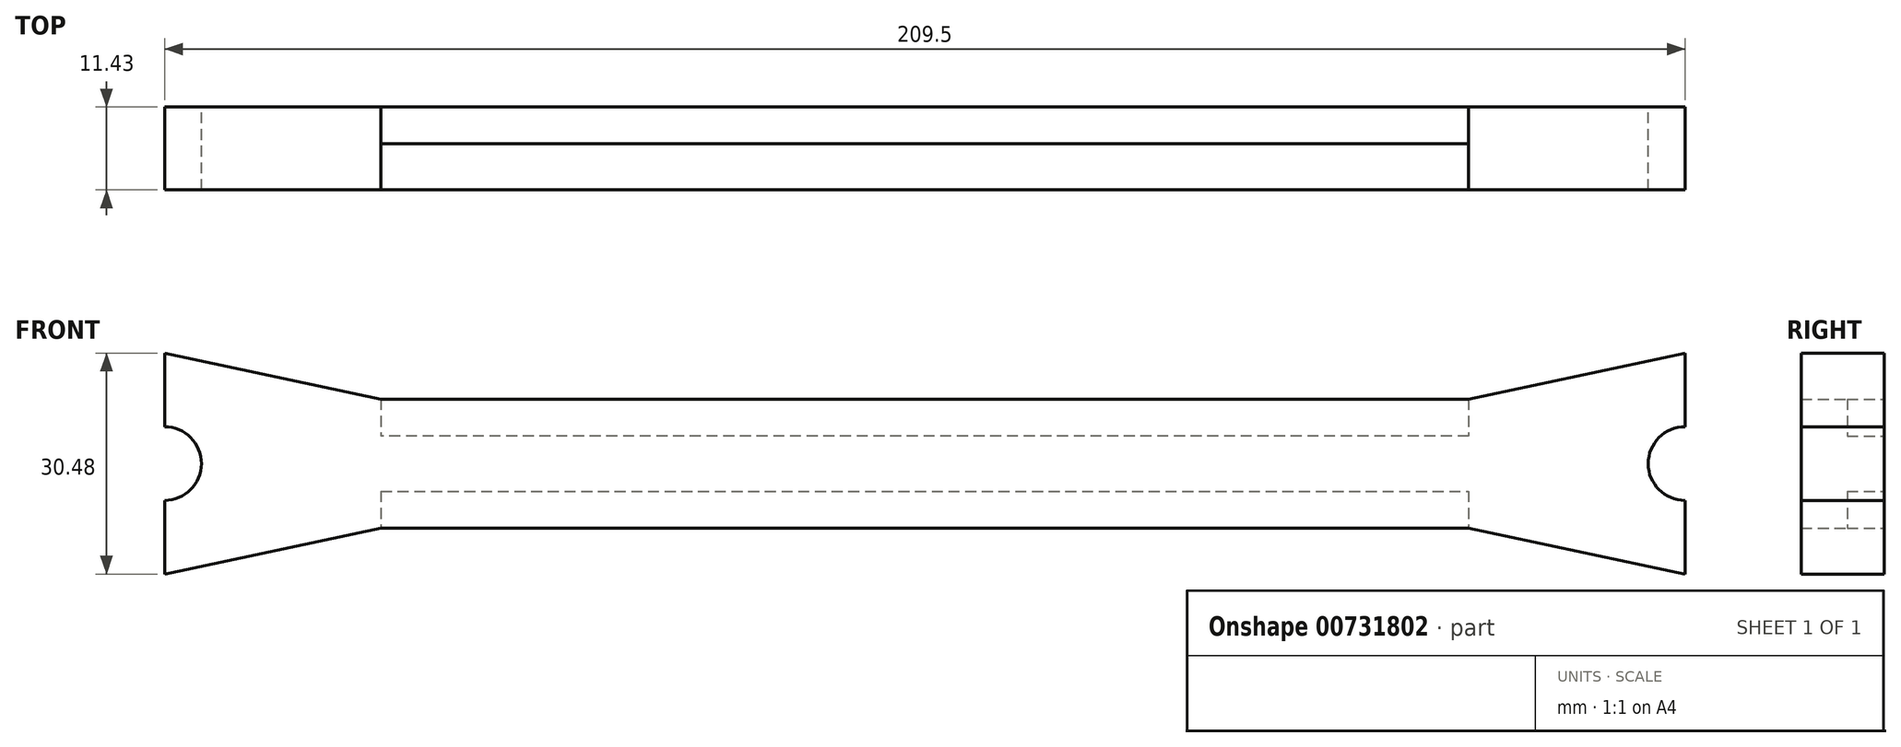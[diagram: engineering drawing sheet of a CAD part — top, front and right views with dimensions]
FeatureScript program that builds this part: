
annotation { "Feature Type Name" : "Feature", "Feature Type Description" : "" }
export const myFeature = defineFeature(function(context is Context, id is Id, definition is map)
    precondition{}
    {
        {
            var Q0;
            Q0=qCreatedBy(makeId("Front.planeOp"),FACE);
            var sketch = newSketch(context, id + "F0", { "sketchPlane" : qUnion([Q0])});
            skLineSegment(sketch, "E0", {"start": v(9.71, 24.9) * mm, "end": v(-140.15, 24.9) * mm});
            skLineSegment(sketch, "E1", {"start": v(-140.15, 42.68) * mm, "end": v(9.71, 42.68) * mm});
            skLineSegment(sketch, "E2", {"start": v(9.71, 42.68) * mm, "end": v(9.71, 24.9) * mm});
            skLineSegment(sketch, "E3", {"start": v(-140.15, 42.68) * mm, "end": v(-140.15, 24.9) * mm});
            skLineSegment(sketch, "E4", {"start": v(-140.15, 33.79) * mm, "end": v(-169.97, 33.79) * mm});
            skCircle(sketch, "E5", {"center": v(-169.97, 33.79) * mm, "radius": 15.24 * mm});
            skLineSegment(sketch, "E6", {"start": v(-169.97, 33.79) * mm, "end": v(-169.97, 18.55) * mm});
            skLineSegment(sketch, "E7", {"start": v(-169.97, 18.55) * mm, "end": v(-169.97, 49.03) * mm});
            skLineSegment(sketch, "E8", {"start": v(-169.97, 18.55) * mm, "end": v(-140.15, 24.9) * mm});
            skLineSegment(sketch, "E9", {"start": v(9.71, 33.79) * mm, "end": v(39.53, 33.79) * mm});
            skCircle(sketch, "E10", {"center": v(39.53, 33.79) * mm, "radius": 15.24 * mm});
            skLineSegment(sketch, "E11", {"start": v(39.53, 33.79) * mm, "end": v(39.53, 18.55) * mm});
            skLineSegment(sketch, "E12", {"start": v(39.53, 18.55) * mm, "end": v(39.53, 49.03) * mm});
            skLineSegment(sketch, "E13", {"start": v(39.53, 49.03) * mm, "end": v(9.71, 42.68) * mm});
            skLineSegment(sketch, "E14", {"start": v(39.53, 18.55) * mm, "end": v(9.71, 24.9) * mm});
            skLineSegment(sketch, "E15", {"start": v(-169.97, 49.03) * mm, "end": v(-140.15, 42.68) * mm});
            skLineSegment(sketch, "E16", {"start": v(-169.97, 33.79) * mm, "end": v(-157.27, 33.79) * mm});
            skLineSegment(sketch, "E17", {"start": v(-157.27, 33.79) * mm, "end": v(-157.27, 29.98) * mm});
            skLineSegment(sketch, "E18", {"start": v(-157.27, 29.98) * mm, "end": v(-157.27, 37.6) * mm});
            skLineSegment(sketch, "E19", {"start": v(-157.27, 37.6) * mm, "end": v(-120.77, 37.6) * mm});
            skLineSegment(sketch, "E20", {"start": v(-157.27, 29.98) * mm, "end": v(-120.77, 29.98) * mm});
            skLineSegment(sketch, "E21", {"start": v(39.53, 33.79) * mm, "end": v(26.83, 33.79) * mm});
            skLineSegment(sketch, "E22", {"start": v(26.83, 33.79) * mm, "end": v(26.83, 29.98) * mm});
            skLineSegment(sketch, "E23", {"start": v(26.83, 29.98) * mm, "end": v(26.83, 37.6) * mm});
            skLineSegment(sketch, "E24", {"start": v(26.83, 37.6) * mm, "end": v(-120.77, 37.6) * mm});
            skLineSegment(sketch, "E25", {"start": v(-120.77, 29.98) * mm, "end": v(26.83, 29.98) * mm});
            skCircle(sketch, "E26", {"center": v(39.53, 33.79) * mm, "radius": 5.08 * mm});
            skCircle(sketch, "E27", {"center": v(-169.97, 33.79) * mm, "radius": 5.08 * mm});
            skSolve(sketch);
        }
        {
            var Q0;
            {var subQ0=sQuery(id+"F0.wireOp",EDGE,"E7");var subQ4=sQuery(id+"F0.wireOp",EDGE,"E27");var subQ5=makeQuery(id+"F0.imprint","INTERSECT",VERTEX,{"disambiguationData":[OD(0.0)],"derivedFrom":[subQ0,subQ4]});Q0=makeQuery(id+"F0.imprint","IMPRINT",FACE,{"disambiguationData":[TD([[makeQuery(id+"F0.imprint","IMPRINT",EDGE,{"disambiguationData":[TD([[subQ5,1.0]])],"derivedFrom":subQ4}),-1.0]])]});}
            var Q1;
            {var subQ7=sQuery(id+"F0.wireOp",EDGE,"E15");var subQ8=sQuery(id+"F0.wireOp",EDGE,"E5");var subQ10=makeQuery(id+"F0.imprint","INTERSECT",VERTEX,{"derivedFrom":[subQ8,subQ7]});Q1=makeQuery(id+"F0.imprint","IMPRINT",FACE,{"disambiguationData":[TD([[makeQuery(id+"F0.imprint","IMPRINT",EDGE,{"disambiguationData":[TD([[subQ10,1.0]])],"derivedFrom":subQ8}),1.0]])]});}
            var Q2;
            {var subQ5=sQuery(id+"F0.wireOp",EDGE,"E8");var subQ7=sQuery(id+"F0.wireOp",EDGE,"E5");var subQ9=makeQuery(id+"F0.imprint","INTERSECT",VERTEX,{"derivedFrom":[subQ7,subQ5]});Q2=makeQuery(id+"F0.imprint","IMPRINT",FACE,{"disambiguationData":[TD([[makeQuery(id+"F0.imprint","IMPRINT",EDGE,{"disambiguationData":[TD([[subQ9,-1.0]])],"derivedFrom":subQ7}),1.0]])]});}
            var Q3;
            {var subQ1=sQuery(id+"F0.wireOp",EDGE,"E4");var subQ3=sQuery(id+"F0.wireOp",EDGE,"E5");var subQ4=makeQuery(id+"F0.imprint","INTERSECT",VERTEX,{"derivedFrom":[subQ1,subQ3]});Q3=makeQuery(id+"F0.imprint","IMPRINT",FACE,{"disambiguationData":[TD([[makeQuery(id+"F0.imprint","IMPRINT",EDGE,{"disambiguationData":[TD([[subQ4,-1.0]])],"derivedFrom":subQ3}),1.0]])]});}
            var Q4;
            {var subQ1=sQuery(id+"F0.wireOp",EDGE,"E4");var subQ3=sQuery(id+"F0.wireOp",EDGE,"E5");var subQ4=makeQuery(id+"F0.imprint","INTERSECT",VERTEX,{"derivedFrom":[subQ1,subQ3]});Q4=makeQuery(id+"F0.imprint","IMPRINT",FACE,{"disambiguationData":[TD([[makeQuery(id+"F0.imprint","IMPRINT",EDGE,{"disambiguationData":[TD([[subQ4,1.0]])],"derivedFrom":subQ3}),1.0]])]});}
            var Q5;
            {var subQ0=sQuery(id+"F0.wireOp",EDGE,"E4");var subQ1=sQuery(id+"F0.wireOp",EDGE,"E3");var subQ2=makeQuery(id+"F0.imprint","INTERSECT",VERTEX,{"derivedFrom":[subQ1,subQ0]});Q5=makeQuery(id+"F0.imprint","IMPRINT",FACE,{"disambiguationData":[TD([[makeQuery(id+"F0.imprint","IMPRINT",EDGE,{"disambiguationData":[TD([[subQ2,-1.0]])],"derivedFrom":subQ1}),-1.0]])]});}
            var Q6;
            {var subQ0=sQuery(id+"F0.wireOp",EDGE,"E4");var subQ1=sQuery(id+"F0.wireOp",EDGE,"E3");var subQ2=makeQuery(id+"F0.imprint","INTERSECT",VERTEX,{"derivedFrom":[subQ1,subQ0]});Q6=makeQuery(id+"F0.imprint","IMPRINT",FACE,{"disambiguationData":[TD([[makeQuery(id+"F0.imprint","IMPRINT",EDGE,{"disambiguationData":[TD([[subQ2,1.0]])],"derivedFrom":subQ1}),-1.0]])]});}
            var Q7;
            {var subQ4=sQuery(id+"F0.wireOp",EDGE,"E2");var subQ5=makeQuery(id+"F0.imprint","INTERSECT",VERTEX,{"derivedFrom":[subQ4,sQuery(id+"F0.wireOp",EDGE,"E9")]});Q7=makeQuery(id+"F0.imprint","IMPRINT",FACE,{"disambiguationData":[TD([[makeQuery(id+"F0.imprint","IMPRINT",EDGE,{"disambiguationData":[TD([[subQ5,1.0]])],"derivedFrom":subQ4}),-1.0]])]});}
            var Q8;
            {var subQ0=sQuery(id+"F0.wireOp",EDGE,"E9");var subQ1=sQuery(id+"F0.wireOp",EDGE,"E2");var subQ2=makeQuery(id+"F0.imprint","INTERSECT",VERTEX,{"derivedFrom":[subQ1,subQ0]});Q8=makeQuery(id+"F0.imprint","IMPRINT",FACE,{"disambiguationData":[TD([[makeQuery(id+"F0.imprint","IMPRINT",EDGE,{"disambiguationData":[TD([[subQ2,1.0]])],"derivedFrom":subQ1}),1.0]])]});}
            var Q9;
            {var subQ0=sQuery(id+"F0.wireOp",EDGE,"E9");var subQ1=sQuery(id+"F0.wireOp",EDGE,"E2");var subQ2=makeQuery(id+"F0.imprint","INTERSECT",VERTEX,{"derivedFrom":[subQ1,subQ0]});Q9=makeQuery(id+"F0.imprint","IMPRINT",FACE,{"disambiguationData":[TD([[makeQuery(id+"F0.imprint","IMPRINT",EDGE,{"disambiguationData":[TD([[subQ2,-1.0]])],"derivedFrom":subQ1}),1.0]])]});}
            var Q10;
            {var subQ1=sQuery(id+"F0.wireOp",EDGE,"E9");var subQ3=sQuery(id+"F0.wireOp",EDGE,"E10");var subQ4=makeQuery(id+"F0.imprint","INTERSECT",VERTEX,{"derivedFrom":[subQ1,subQ3]});Q10=makeQuery(id+"F0.imprint","IMPRINT",FACE,{"disambiguationData":[TD([[makeQuery(id+"F0.imprint","IMPRINT",EDGE,{"disambiguationData":[TD([[subQ4,1.0]])],"derivedFrom":subQ3}),1.0]])]});}
            var Q11;
            {var subQ1=sQuery(id+"F0.wireOp",EDGE,"E9");var subQ3=sQuery(id+"F0.wireOp",EDGE,"E10");var subQ4=makeQuery(id+"F0.imprint","INTERSECT",VERTEX,{"derivedFrom":[subQ1,subQ3]});Q11=makeQuery(id+"F0.imprint","IMPRINT",FACE,{"disambiguationData":[TD([[makeQuery(id+"F0.imprint","IMPRINT",EDGE,{"disambiguationData":[TD([[subQ4,-1.0]])],"derivedFrom":subQ3}),1.0]])]});}
            var Q12;
            {var subQ5=sQuery(id+"F0.wireOp",EDGE,"E13");var subQ7=sQuery(id+"F0.wireOp",EDGE,"E10");var subQ10=makeQuery(id+"F0.imprint","INTERSECT",VERTEX,{"derivedFrom":[subQ7,subQ5]});Q12=makeQuery(id+"F0.imprint","IMPRINT",FACE,{"disambiguationData":[TD([[makeQuery(id+"F0.imprint","IMPRINT",EDGE,{"disambiguationData":[TD([[subQ10,-1.0]])],"derivedFrom":subQ7}),1.0]])]});}
            var Q13;
            {var subQ0=sQuery(id+"F0.wireOp",EDGE,"E12");var subQ4=sQuery(id+"F0.wireOp",EDGE,"E26");var subQ5=makeQuery(id+"F0.imprint","INTERSECT",VERTEX,{"disambiguationData":[OD(0.0)],"derivedFrom":[subQ0,subQ4]});Q13=makeQuery(id+"F0.imprint","IMPRINT",FACE,{"disambiguationData":[TD([[makeQuery(id+"F0.imprint","IMPRINT",EDGE,{"disambiguationData":[TD([[subQ5,-1.0]])],"derivedFrom":subQ4}),-1.0]])]});}
            var Q14;
            {var subQ5=sQuery(id+"F0.wireOp",EDGE,"E14");var subQ7=sQuery(id+"F0.wireOp",EDGE,"E10");var subQ9=makeQuery(id+"F0.imprint","INTERSECT",VERTEX,{"derivedFrom":[subQ7,subQ5]});Q14=makeQuery(id+"F0.imprint","IMPRINT",FACE,{"disambiguationData":[TD([[makeQuery(id+"F0.imprint","IMPRINT",EDGE,{"disambiguationData":[TD([[subQ9,1.0]])],"derivedFrom":subQ7}),1.0]])]});}
            var Q15;
            {var subQ0=sQuery(id+"F0.wireOp",EDGE,"E13");var subQ5=sQuery(id+"F0.wireOp",EDGE,"E10");var subQ6=makeQuery(id+"F0.imprint","INTERSECT",VERTEX,{"derivedFrom":[subQ5,subQ0]});Q15=makeQuery(id+"F0.imprint","IMPRINT",FACE,{"disambiguationData":[TD([[makeQuery(id+"F0.imprint","IMPRINT",EDGE,{"disambiguationData":[TD([[subQ6,-1.0]])],"derivedFrom":subQ5}),-1.0]])]});}
            var Q16;
            {var subQ0=sQuery(id+"F0.wireOp",EDGE,"E14");var subQ5=sQuery(id+"F0.wireOp",EDGE,"E10");var subQ6=makeQuery(id+"F0.imprint","INTERSECT",VERTEX,{"derivedFrom":[subQ5,subQ0]});Q16=makeQuery(id+"F0.imprint","IMPRINT",FACE,{"disambiguationData":[TD([[makeQuery(id+"F0.imprint","IMPRINT",EDGE,{"disambiguationData":[TD([[subQ6,1.0]])],"derivedFrom":subQ5}),-1.0]])]});}
            var Q17;
            {var subQ0=sQuery(id+"F0.wireOp",EDGE,"E8");var subQ5=sQuery(id+"F0.wireOp",EDGE,"E5");var subQ6=makeQuery(id+"F0.imprint","INTERSECT",VERTEX,{"derivedFrom":[subQ5,subQ0]});Q17=makeQuery(id+"F0.imprint","IMPRINT",FACE,{"disambiguationData":[TD([[makeQuery(id+"F0.imprint","IMPRINT",EDGE,{"disambiguationData":[TD([[subQ6,-1.0]])],"derivedFrom":subQ5}),-1.0]])]});}
            var Q18;
            {var subQ0=sQuery(id+"F0.wireOp",EDGE,"E15");var subQ5=sQuery(id+"F0.wireOp",EDGE,"E5");var subQ6=makeQuery(id+"F0.imprint","INTERSECT",VERTEX,{"derivedFrom":[subQ5,subQ0]});Q18=makeQuery(id+"F0.imprint","IMPRINT",FACE,{"disambiguationData":[TD([[makeQuery(id+"F0.imprint","IMPRINT",EDGE,{"disambiguationData":[TD([[subQ6,1.0]])],"derivedFrom":subQ5}),-1.0]])]});}
            extrude(context, id + "F1", {"entities" : qUnion([Q0, Q1, Q2, Q3, Q4, Q5, Q6, Q7, Q8, Q9, Q10, Q11, Q12, Q13, Q14, Q15, Q16, Q17, Q18]), "depth" : 11.43 * mm, "offsetDistance" : 25.4 * mm});
        }
        {
            var Q0;
            Q0=makeQuery(id+"F1.opExtrude","CAP_FACE",FACE,{"disambiguationData":[OSD([sQuery(id+"F0.wireOp",EDGE,"E2"),sQuery(id+"F0.wireOp",EDGE,"E3"),sQuery(id+"F0.wireOp",EDGE,"E5"),sQuery(id+"F0.wireOp",EDGE,"E8"),sQuery(id+"F0.wireOp",EDGE,"E10"),sQuery(id+"F0.wireOp",EDGE,"E13"),sQuery(id+"F0.wireOp",EDGE,"E14"),sQuery(id+"F0.wireOp",EDGE,"E15"),sQuery(id+"F0.wireOp",EDGE,"E19"),sQuery(id+"F0.wireOp",EDGE,"E20"),sQuery(id+"F0.wireOp",EDGE,"E24"),sQuery(id+"F0.wireOp",EDGE,"E25"),sQuery(id+"F0.wireOp",EDGE,"E26"),sQuery(id+"F0.wireOp",EDGE,"E27")])],"isStart":false});
            var sketch = newSketch(context, id + "F2", { "sketchPlane" : qUnion([Q0])});
            skLineSegment(sketch, "E28", {"start": v(-140.15, 24.9) * mm, "end": v(9.71, 24.9) * mm});
            skLineSegment(sketch, "E29", {"start": v(9.71, 24.9) * mm, "end": v(9.71, 42.68) * mm});
            skLineSegment(sketch, "E30", {"start": v(9.71, 42.68) * mm, "end": v(-140.15, 42.68) * mm});
            skLineSegment(sketch, "E31", {"start": v(-140.15, 42.68) * mm, "end": v(-140.15, 24.9) * mm});
            skLineSegment(sketch, "E32", {"start": v(-140.15, 37.6) * mm, "end": v(9.71, 37.6) * mm});
            skLineSegment(sketch, "E33", {"start": v(9.71, 37.6) * mm, "end": v(9.71, 29.98) * mm});
            skLineSegment(sketch, "E34", {"start": v(9.71, 29.98) * mm, "end": v(-140.15, 29.98) * mm});
            skSolve(sketch);
        }
        {
            var Q0;
            {var subQ0=sQuery(id+"F2.wireOp",EDGE,"E30");Q0=makeQuery(id+"F2.imprint","IMPRINT",FACE,{"disambiguationData":[TD([[makeQuery(id+"F2.imprint","IMPRINT",EDGE,{"derivedFrom":subQ0}),1.0]])]});}
            var Q1;
            {var subQ0=sQuery(id+"F2.wireOp",EDGE,"E28");Q1=makeQuery(id+"F2.imprint","IMPRINT",FACE,{"disambiguationData":[TD([[makeQuery(id+"F2.imprint","IMPRINT",EDGE,{"derivedFrom":subQ0}),1.0]])]});}
            extrude(context, id + "F3", {"entities" : qUnion([Q0, Q1]), "operationType" : NewBodyOperationType.ADD, "depth" : -6.35 * mm, "offsetDistance" : 25.4 * mm});
        }
    });
